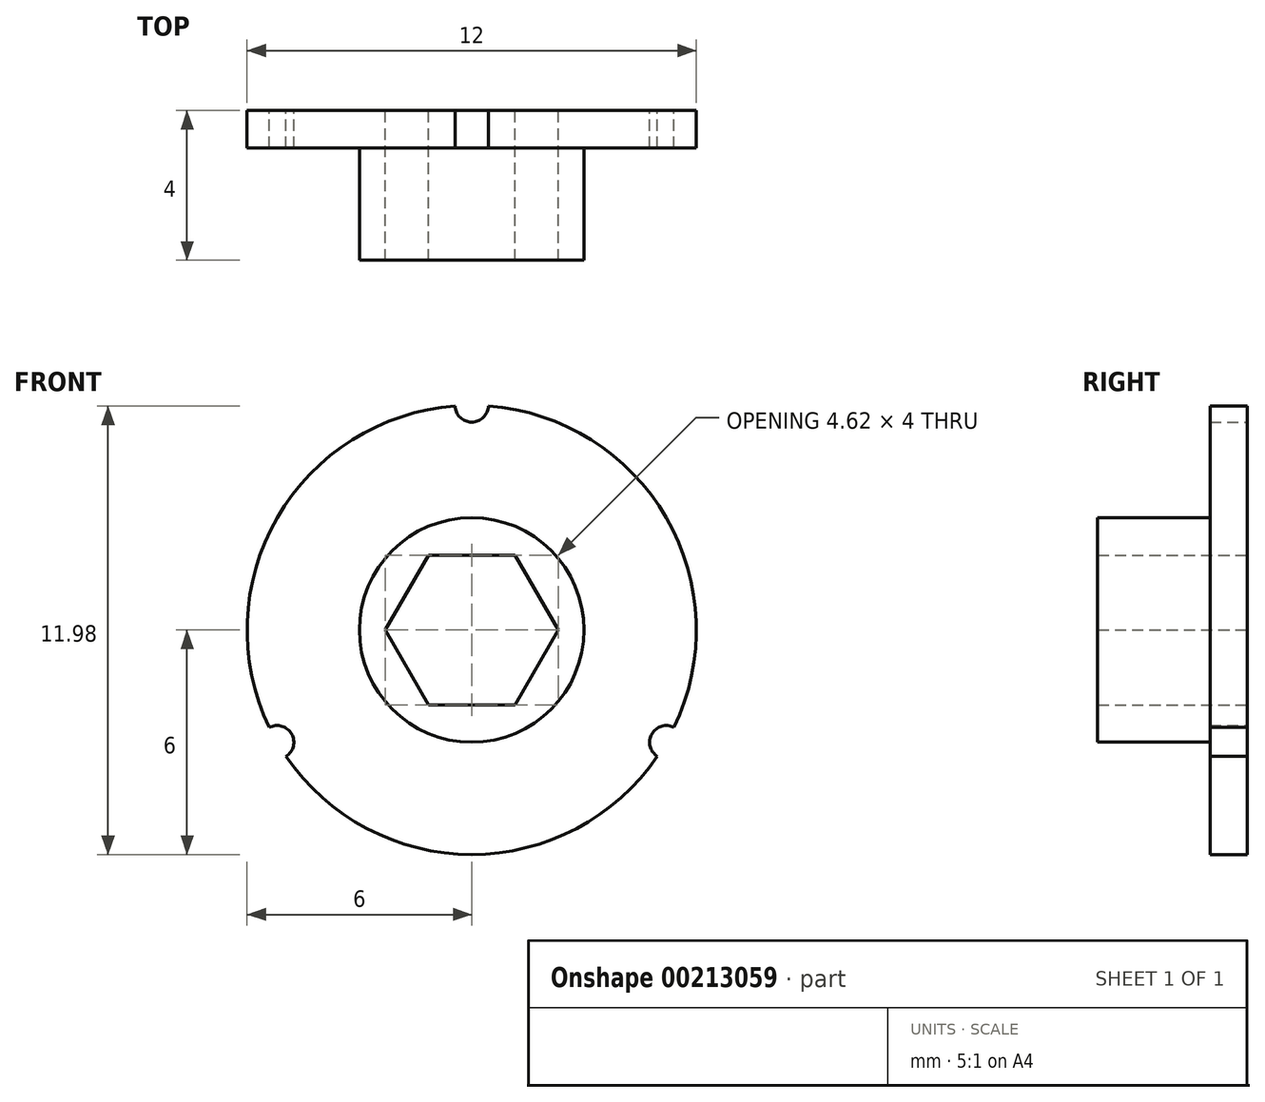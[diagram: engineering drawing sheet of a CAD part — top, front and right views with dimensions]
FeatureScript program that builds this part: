
annotation { "Feature Type Name" : "Feature", "Feature Type Description" : "" }
export const myFeature = defineFeature(function(context is Context, id is Id, definition is map)
    precondition{}
    {
        {
            var Q0;
            Q0=qCreatedBy(makeId("Front.planeOp"),FACE);
            var sketch = newSketch(context, id + "F0", { "sketchPlane" : qUnion([Q0])});
            skCircle(sketch, "E0.cCircle", {"center": v(0, 0) * mm, "radius": 2 * mm, "construction": true});
            skLineSegment(sketch, "E0.0", {"start": v(-1.15, 2) * mm, "end": v(1.15, 2) * mm});
            skLineSegment(sketch, "E0.1", {"start": v(1.15, 2) * mm, "end": v(2.3, 0) * mm});
            skLineSegment(sketch, "E0.2", {"start": v(2.3, 0) * mm, "end": v(1.15, -2) * mm});
            skLineSegment(sketch, "E0.3", {"start": v(1.15, -2) * mm, "end": v(-1.15, -2) * mm});
            skLineSegment(sketch, "E0.4", {"start": v(-1.15, -2) * mm, "end": v(-2.3, 0) * mm});
            skLineSegment(sketch, "E0.5", {"start": v(-2.3, 0) * mm, "end": v(-1.15, 2) * mm});
            skPoint(sketch, "E0.0.midPoint", {"position": v(0, 2) * mm});
            skCircle(sketch, "E1", {"center": v(0, 0) * mm, "radius": 3 * mm});
            skCircle(sketch, "E2", {"center": v(0, 0) * mm, "radius": 6 * mm});
            skCircle(sketch, "E3", {"center": v(0, 6) * mm, "radius": 0.45 * mm});
            skCircle(sketch, "E4.1.0", {"center": v(-5.2, -3) * mm, "radius": 0.45 * mm});
            skCircle(sketch, "E4.2.0", {"center": v(5.2, -3) * mm, "radius": 0.45 * mm});
            skSolve(sketch);
        }
        {
            var Q0;
            Q0=makeQuery(id+"F0.imprint","IMPRINT",FACE,{"disambiguationData":[TD([[makeQuery(id+"F0.imprint","IMPRINT",EDGE,{"derivedFrom":sQuery(id+"F0.wireOp",EDGE,"E1")}),-1.0]])]});
            extrude(context, id + "F1", {"entities" : qUnion([Q0]), "depth" : 1 * mm});
        }
        {
            var Q0;
            Q0=makeQuery(id+"F0.imprint","IMPRINT",FACE,{"disambiguationData":[TD([[makeQuery(id+"F0.imprint","IMPRINT",EDGE,{"derivedFrom":sQuery(id+"F0.wireOp",EDGE,"E0.0")}),1.0]])]});
            extrude(context, id + "F2", {"entities" : qUnion([Q0]), "operationType" : NewBodyOperationType.ADD, "depth" : 4 * mm});
        }
    });
